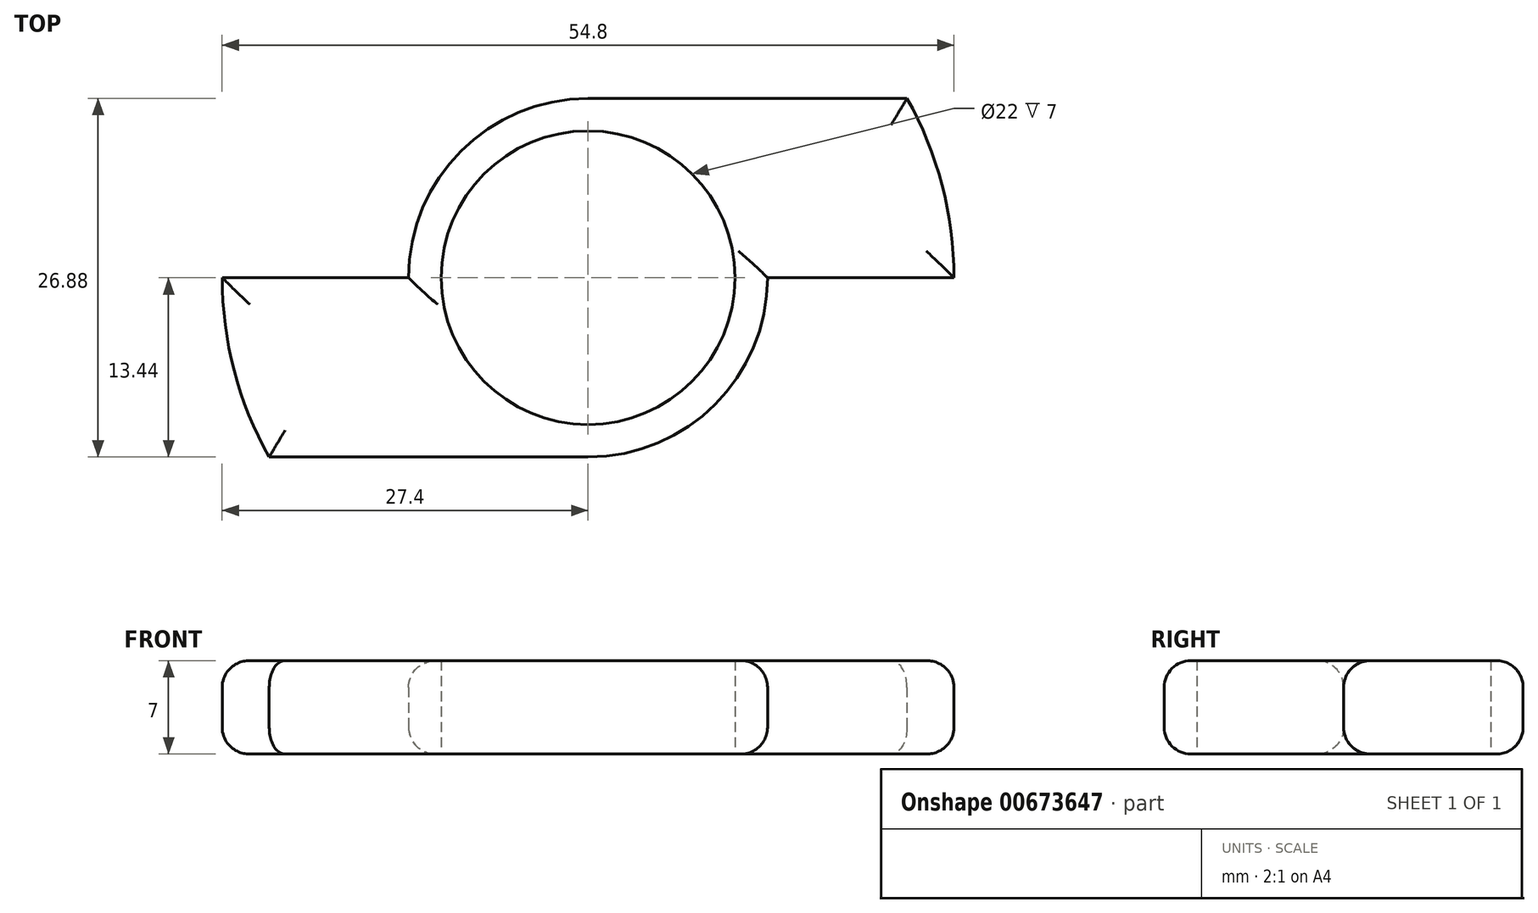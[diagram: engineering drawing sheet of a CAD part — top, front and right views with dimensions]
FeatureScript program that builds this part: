
annotation { "Feature Type Name" : "Feature", "Feature Type Description" : "" }
export const myFeature = defineFeature(function(context is Context, id is Id, definition is map)
    precondition{}
    {
        {
            var Q0;
            Q0=qCreatedBy(makeId("Top.planeOp"),FACE);
            var sketch = newSketch(context, id + "F0", { "sketchPlane" : qUnion([Q0])});
            skCircle(sketch, "E0", {"center": v(0, 0) * mm, "radius": 11 * mm});
            skCircle(sketch, "E1", {"center": v(0, 0) * mm, "radius": 27.4 * mm});
            skLineSegment(sketch, "E2", {"start": v(0, 0) * mm, "end": v(-27.4, 0) * mm});
            skLineSegment(sketch, "E3", {"start": v(0, 0) * mm, "end": v(27.4, 0) * mm});
            skLineSegment(sketch, "E4", {"start": v(0, 0) * mm, "end": v(0, 27.4) * mm});
            skLineSegment(sketch, "E5", {"start": v(0, 0) * mm, "end": v(0, -27.4) * mm});
            skLineSegment(sketch, "E6", {"start": v(0, -11) * mm, "end": v(25.1, -11) * mm});
            skLineSegment(sketch, "E7", {"start": v(0, 11) * mm, "end": v(25.1, 11) * mm});
            skLineSegment(sketch, "E8", {"start": v(0, -11) * mm, "end": v(-25.1, -11) * mm});
            skLineSegment(sketch, "E9", {"start": v(0, 11) * mm, "end": v(-25.1, 11) * mm});
            skCircle(sketch, "E10", {"center": v(0, 0) * mm, "radius": 13.44 * mm});
            skLineSegment(sketch, "E11", {"start": v(0, 13.44) * mm, "end": v(23.88, 13.44) * mm});
            skPoint(sketch, "E11.startSnap0", {"position": v(0, 13.7) * mm});
            skLineSegment(sketch, "E12", {"start": v(0, -13.44) * mm, "end": v(23.88, -13.44) * mm});
            skLineSegment(sketch, "E13", {"start": v(0, -13.44) * mm, "end": v(-23.88, -13.44) * mm});
            skLineSegment(sketch, "E14", {"start": v(0, 13.7) * mm, "end": v(-23.73, 13.7) * mm});
            skSolve(sketch);
        }
        {
            var Q0;
            {var subQ1=sQuery(id+"F0.wireOp",EDGE,"E0");var subQ3=sQuery(id+"F0.wireOp",EDGE,"E2");var subQ4=makeQuery(id+"F0.imprint","INTERSECT",VERTEX,{"derivedFrom":[subQ1,subQ3]});Q0=makeQuery(id+"F0.imprint","IMPRINT",FACE,{"disambiguationData":[TD([[makeQuery(id+"F0.imprint","IMPRINT",EDGE,{"disambiguationData":[TD([[subQ4,-1.0]])],"derivedFrom":subQ3}),-1.0]])]});}
            var Q1;
            {var subQ1=sQuery(id+"F0.wireOp",EDGE,"E0");var subQ3=sQuery(id+"F0.wireOp",EDGE,"E3");var subQ4=makeQuery(id+"F0.imprint","INTERSECT",VERTEX,{"derivedFrom":[subQ1,subQ3]});Q1=makeQuery(id+"F0.imprint","IMPRINT",FACE,{"disambiguationData":[TD([[makeQuery(id+"F0.imprint","IMPRINT",EDGE,{"disambiguationData":[TD([[subQ4,-1.0]])],"derivedFrom":subQ3}),1.0]])]});}
            var Q2;
            {var subQ1=sQuery(id+"F0.wireOp",EDGE,"E0");var subQ3=sQuery(id+"F0.wireOp",EDGE,"E3");var subQ4=makeQuery(id+"F0.imprint","INTERSECT",VERTEX,{"derivedFrom":[subQ1,subQ3]});Q2=makeQuery(id+"F0.imprint","IMPRINT",FACE,{"disambiguationData":[TD([[makeQuery(id+"F0.imprint","IMPRINT",EDGE,{"disambiguationData":[TD([[subQ4,-1.0]])],"derivedFrom":subQ3}),-1.0]])]});}
            var Q3;
            {var subQ0=sQuery(id+"F0.wireOp",EDGE,"E6");var subQ3=sQuery(id+"F0.wireOp",EDGE,"E10");var subQ5=makeQuery(id+"F0.imprint","INTERSECT",VERTEX,{"derivedFrom":[subQ0,subQ3]});Q3=makeQuery(id+"F0.imprint","IMPRINT",FACE,{"disambiguationData":[TD([[makeQuery(id+"F0.imprint","IMPRINT",EDGE,{"disambiguationData":[TD([[subQ5,1.0]])],"derivedFrom":subQ0}),-1.0]])]});}
            var Q4;
            {var subQ0=sQuery(id+"F0.wireOp",EDGE,"E8");var subQ3=sQuery(id+"F0.wireOp",EDGE,"E10");var subQ5=makeQuery(id+"F0.imprint","INTERSECT",VERTEX,{"derivedFrom":[subQ0,subQ3]});Q4=makeQuery(id+"F0.imprint","IMPRINT",FACE,{"disambiguationData":[TD([[makeQuery(id+"F0.imprint","IMPRINT",EDGE,{"disambiguationData":[TD([[subQ5,1.0]])],"derivedFrom":subQ0}),1.0]])]});}
            var Q5;
            {var subQ1=sQuery(id+"F0.wireOp",EDGE,"E0");var subQ3=sQuery(id+"F0.wireOp",EDGE,"E2");var subQ4=makeQuery(id+"F0.imprint","INTERSECT",VERTEX,{"derivedFrom":[subQ1,subQ3]});Q5=makeQuery(id+"F0.imprint","IMPRINT",FACE,{"disambiguationData":[TD([[makeQuery(id+"F0.imprint","IMPRINT",EDGE,{"disambiguationData":[TD([[subQ4,-1.0]])],"derivedFrom":subQ3}),1.0]])]});}
            var Q6;
            {var subQ0=sQuery(id+"F0.wireOp",EDGE,"E2");var subQ1=sQuery(id+"F0.wireOp",EDGE,"E1");var subQ2=makeQuery(id+"F0.imprint","INTERSECT",VERTEX,{"derivedFrom":[subQ1,subQ0]});Q6=makeQuery(id+"F0.imprint","IMPRINT",FACE,{"disambiguationData":[TD([[makeQuery(id+"F0.imprint","IMPRINT",EDGE,{"disambiguationData":[TD([[subQ2,-1.0]])],"derivedFrom":subQ1}),1.0]])]});}
            var Q7;
            {var subQ0=sQuery(id+"F0.wireOp",EDGE,"E3");var subQ1=sQuery(id+"F0.wireOp",EDGE,"E1");var subQ2=makeQuery(id+"F0.imprint","INTERSECT",VERTEX,{"derivedFrom":[subQ1,subQ0]});Q7=makeQuery(id+"F0.imprint","IMPRINT",FACE,{"disambiguationData":[TD([[makeQuery(id+"F0.imprint","IMPRINT",EDGE,{"disambiguationData":[TD([[subQ2,-1.0]])],"derivedFrom":subQ1}),1.0]])]});}
            var Q8;
            {var subQ0=sQuery(id+"F0.wireOp",EDGE,"E7");var subQ3=sQuery(id+"F0.wireOp",EDGE,"E10");var subQ5=makeQuery(id+"F0.imprint","INTERSECT",VERTEX,{"derivedFrom":[subQ0,subQ3]});Q8=makeQuery(id+"F0.imprint","IMPRINT",FACE,{"disambiguationData":[TD([[makeQuery(id+"F0.imprint","IMPRINT",EDGE,{"disambiguationData":[TD([[subQ5,-1.0]])],"derivedFrom":subQ3}),1.0]])]});}
            var Q9;
            {var subQ0=sQuery(id+"F0.wireOp",EDGE,"E9");var subQ3=sQuery(id+"F0.wireOp",EDGE,"E10");var subQ5=makeQuery(id+"F0.imprint","INTERSECT",VERTEX,{"derivedFrom":[subQ0,subQ3]});Q9=makeQuery(id+"F0.imprint","IMPRINT",FACE,{"disambiguationData":[TD([[makeQuery(id+"F0.imprint","IMPRINT",EDGE,{"disambiguationData":[TD([[subQ5,1.0]])],"derivedFrom":subQ3}),1.0]])]});}
            var Q10;
            {var subQ3=sQuery(id+"F0.wireOp",EDGE,"E13");Q10=makeQuery(id+"F0.imprint","IMPRINT",FACE,{"disambiguationData":[TD([[makeQuery(id+"F0.imprint","IMPRINT",EDGE,{"derivedFrom":subQ3}),-1.0]])]});}
            var Q11;
            {var subQ3=sQuery(id+"F0.wireOp",EDGE,"E11");Q11=makeQuery(id+"F0.imprint","IMPRINT",FACE,{"disambiguationData":[TD([[makeQuery(id+"F0.imprint","IMPRINT",EDGE,{"derivedFrom":subQ3}),-1.0]])]});}
            extrude(context, id + "F1", {"entities" : qUnion([Q0, Q1, Q2, Q3, Q4, Q5, Q6, Q7, Q8, Q9, Q10, Q11]), "depth" : 7 * mm, "offsetDistance" : 25.4 * mm});
        }
        {
            var Q0;
            {var subQ0=sQuery(id+"F0.wireOp",EDGE,"E10");var subQ1=makeQuery(id+"F0.imprint","INTERSECT",VERTEX,{"derivedFrom":[sQuery(id+"F0.wireOp",EDGE,"E9"),subQ0]});Q0=makeQuery(id+"F1.opExtrude","CAP_EDGE",EDGE,{"disambiguationData":[OSD([subQ0]),TDD([makeQuery(id+"F0.imprint","IMPRINT",EDGE,{"disambiguationData":[TD([[subQ1,1.0]])],"derivedFrom":subQ0}),makeQuery(id+"F0.imprint","IMPRINT",EDGE,{"disambiguationData":[TD([[makeQuery(id+"F0.imprint","INTERSECT",VERTEX,{"derivedFrom":[sQuery(id+"F0.wireOp",EDGE,"E2"),subQ0]}),1.0]])],"derivedFrom":subQ0})])],"isStart":false});}
            var Q1;
            {var subQ0=sQuery(id+"F0.wireOp",EDGE,"E10");var subQ1=makeQuery(id+"F0.imprint","INTERSECT",VERTEX,{"derivedFrom":[sQuery(id+"F0.wireOp",EDGE,"E6"),subQ0]});Q1=makeQuery(id+"F1.opExtrude","CAP_EDGE",EDGE,{"disambiguationData":[OSD([subQ0]),TDD([makeQuery(id+"F0.imprint","IMPRINT",EDGE,{"disambiguationData":[TD([[subQ1,1.0]])],"derivedFrom":subQ0}),makeQuery(id+"F0.imprint","IMPRINT",EDGE,{"disambiguationData":[TD([[makeQuery(id+"F0.imprint","INTERSECT",VERTEX,{"derivedFrom":[sQuery(id+"F0.wireOp",EDGE,"E3"),subQ0]}),1.0]])],"derivedFrom":subQ0})])],"isStart":false});}
            var Q2;
            Q2=makeQuery(id+"F1.opExtrude","CAP_EDGE",EDGE,{"disambiguationData":[OSD([sQuery(id+"F0.wireOp",EDGE,"E13")])],"isStart":true});
            var Q3;
            {var subQ0=sQuery(id+"F0.wireOp",EDGE,"E1");var subQ1=makeQuery(id+"F0.imprint","INTERSECT",VERTEX,{"derivedFrom":[subQ0,sQuery(id+"F0.wireOp",EDGE,"E8")]});Q3=makeQuery(id+"F1.opExtrude","CAP_EDGE",EDGE,{"disambiguationData":[OSD([subQ0]),TDD([makeQuery(id+"F0.imprint","IMPRINT",EDGE,{"disambiguationData":[TD([[makeQuery(id+"F0.imprint","INTERSECT",VERTEX,{"derivedFrom":[subQ0,sQuery(id+"F0.wireOp",EDGE,"E2")]}),-1.0]])],"derivedFrom":subQ0}),makeQuery(id+"F0.imprint","IMPRINT",EDGE,{"disambiguationData":[TD([[subQ1,-1.0]])],"derivedFrom":subQ0})])],"isStart":true});}
            var Q4;
            Q4=makeQuery(id+"F1.opExtrude","CAP_EDGE",EDGE,{"disambiguationData":[OSD([sQuery(id+"F0.wireOp",EDGE,"E11")])],"isStart":true});
            var Q5;
            {var subQ0=sQuery(id+"F0.wireOp",EDGE,"E1");var subQ1=makeQuery(id+"F0.imprint","INTERSECT",VERTEX,{"derivedFrom":[subQ0,sQuery(id+"F0.wireOp",EDGE,"E7")]});Q5=makeQuery(id+"F1.opExtrude","CAP_EDGE",EDGE,{"disambiguationData":[OSD([subQ0]),TDD([makeQuery(id+"F0.imprint","IMPRINT",EDGE,{"disambiguationData":[TD([[makeQuery(id+"F0.imprint","INTERSECT",VERTEX,{"derivedFrom":[subQ0,sQuery(id+"F0.wireOp",EDGE,"E3")]}),-1.0]])],"derivedFrom":subQ0}),makeQuery(id+"F0.imprint","IMPRINT",EDGE,{"disambiguationData":[TD([[subQ1,-1.0]])],"derivedFrom":subQ0})])],"isStart":true});}
            var Q6;
            Q6=makeQuery(id+"F1.opExtrude","CAP_EDGE",EDGE,{"disambiguationData":[OSD([sQuery(id+"F0.wireOp",EDGE,"E3")])],"isStart":true});
            var Q7;
            Q7=makeQuery(id+"F1.opExtrude","CAP_EDGE",EDGE,{"disambiguationData":[OSD([sQuery(id+"F0.wireOp",EDGE,"E2")])],"isStart":true});
            var Q8;
            {var subQ0=sQuery(id+"F0.wireOp",EDGE,"E1");var subQ1=makeQuery(id+"F0.imprint","INTERSECT",VERTEX,{"derivedFrom":[subQ0,sQuery(id+"F0.wireOp",EDGE,"E7")]});Q8=makeQuery(id+"F1.opExtrude","CAP_EDGE",EDGE,{"disambiguationData":[OSD([subQ0]),TDD([makeQuery(id+"F0.imprint","IMPRINT",EDGE,{"disambiguationData":[TD([[makeQuery(id+"F0.imprint","INTERSECT",VERTEX,{"derivedFrom":[subQ0,sQuery(id+"F0.wireOp",EDGE,"E3")]}),-1.0]])],"derivedFrom":subQ0}),makeQuery(id+"F0.imprint","IMPRINT",EDGE,{"disambiguationData":[TD([[subQ1,-1.0]])],"derivedFrom":subQ0})])],"isStart":false});}
            var Q9;
            {var subQ0=sQuery(id+"F0.wireOp",EDGE,"E1");var subQ1=makeQuery(id+"F0.imprint","INTERSECT",VERTEX,{"derivedFrom":[subQ0,sQuery(id+"F0.wireOp",EDGE,"E8")]});Q9=makeQuery(id+"F1.opExtrude","CAP_EDGE",EDGE,{"disambiguationData":[OSD([subQ0]),TDD([makeQuery(id+"F0.imprint","IMPRINT",EDGE,{"disambiguationData":[TD([[makeQuery(id+"F0.imprint","INTERSECT",VERTEX,{"derivedFrom":[subQ0,sQuery(id+"F0.wireOp",EDGE,"E2")]}),-1.0]])],"derivedFrom":subQ0}),makeQuery(id+"F0.imprint","IMPRINT",EDGE,{"disambiguationData":[TD([[subQ1,-1.0]])],"derivedFrom":subQ0})])],"isStart":false});}
            var Q10;
            Q10=makeQuery(id+"F1.opExtrude","CAP_EDGE",EDGE,{"disambiguationData":[OSD([sQuery(id+"F0.wireOp",EDGE,"E3")])],"isStart":false});
            var Q11;
            Q11=makeQuery(id+"F1.opExtrude","CAP_EDGE",EDGE,{"disambiguationData":[OSD([sQuery(id+"F0.wireOp",EDGE,"E2")])],"isStart":false});
            var Q12;
            Q12=makeQuery(id+"F1.opExtrude","CAP_EDGE",EDGE,{"disambiguationData":[OSD([sQuery(id+"F0.wireOp",EDGE,"E11")])],"isStart":false});
            fillet(context, id + "F2", {"entities" : qUnion([Q0, Q1, Q2, Q3, Q4, Q5, Q6, Q7, Q8, Q9, Q10, Q11, Q12]), "radius" : 2 * mm, "tangentPropagation" : true, "allowEdgeOverflow" : false});
        }
    });
